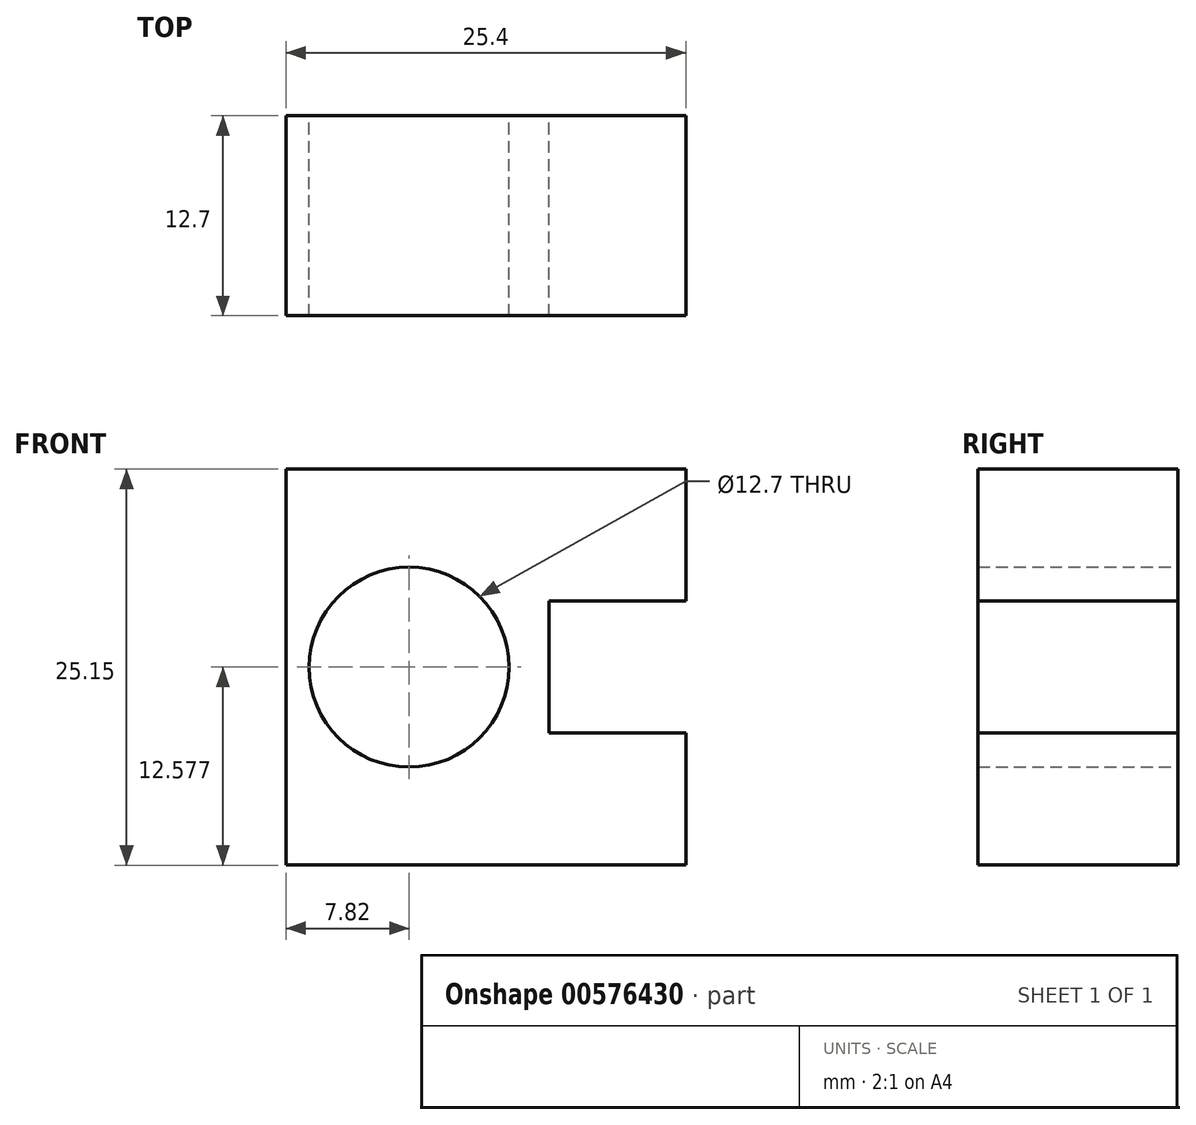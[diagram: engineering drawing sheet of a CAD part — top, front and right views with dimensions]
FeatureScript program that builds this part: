
annotation { "Feature Type Name" : "Feature", "Feature Type Description" : "" }
export const myFeature = defineFeature(function(context is Context, id is Id, definition is map)
    precondition{}
    {
        {
            var Q0;
            Q0=qCreatedBy(makeId("Front.planeOp"),FACE);
            var sketch = newSketch(context, id + "F0", { "sketchPlane" : qUnion([Q0])});
            skLineSegment(sketch, "E0", {"start": v(-29.75, 0) * mm, "end": v(-29.75, -25.15) * mm});
            skLineSegment(sketch, "E1", {"start": v(-29.75, -25.15) * mm, "end": v(-4.35, -25.15) * mm});
            skLineSegment(sketch, "E2", {"start": v(-4.35, -25.15) * mm, "end": v(-4.35, -16.76) * mm});
            skLineSegment(sketch, "E3", {"start": v(-4.35, -16.76) * mm, "end": v(-13.05, -16.76) * mm});
            skLineSegment(sketch, "E4", {"start": v(-13.05, -16.76) * mm, "end": v(-13.05, -8.38) * mm});
            skLineSegment(sketch, "E5", {"start": v(-13.05, -8.38) * mm, "end": v(-4.35, -8.38) * mm});
            skLineSegment(sketch, "E6", {"start": v(-4.35, -8.38) * mm, "end": v(-4.35, 0) * mm});
            skLineSegment(sketch, "E7", {"start": v(-4.35, 0) * mm, "end": v(-29.75, 0) * mm});
            skCircle(sketch, "E8", {"center": v(-21.93, -12.57) * mm, "radius": 6.35 * mm});
            skPoint(sketch, "E8.centerSnap0", {"position": v(-13.05, -12.57) * mm});
            skSolve(sketch);
        }
        {
            var Q0;
            Q0=makeQuery(id+"F0.imprint","IMPRINT",FACE,{"disambiguationData":[TD([[makeQuery(id+"F0.imprint","IMPRINT",EDGE,{"derivedFrom":sQuery(id+"F0.wireOp",EDGE,"E0")}),1.0]])]});
            extrude(context, id + "F1", {"entities" : qUnion([Q0]), "depth" : 12.7 * mm, "offsetDistance" : 25.4 * mm});
        }
    });
